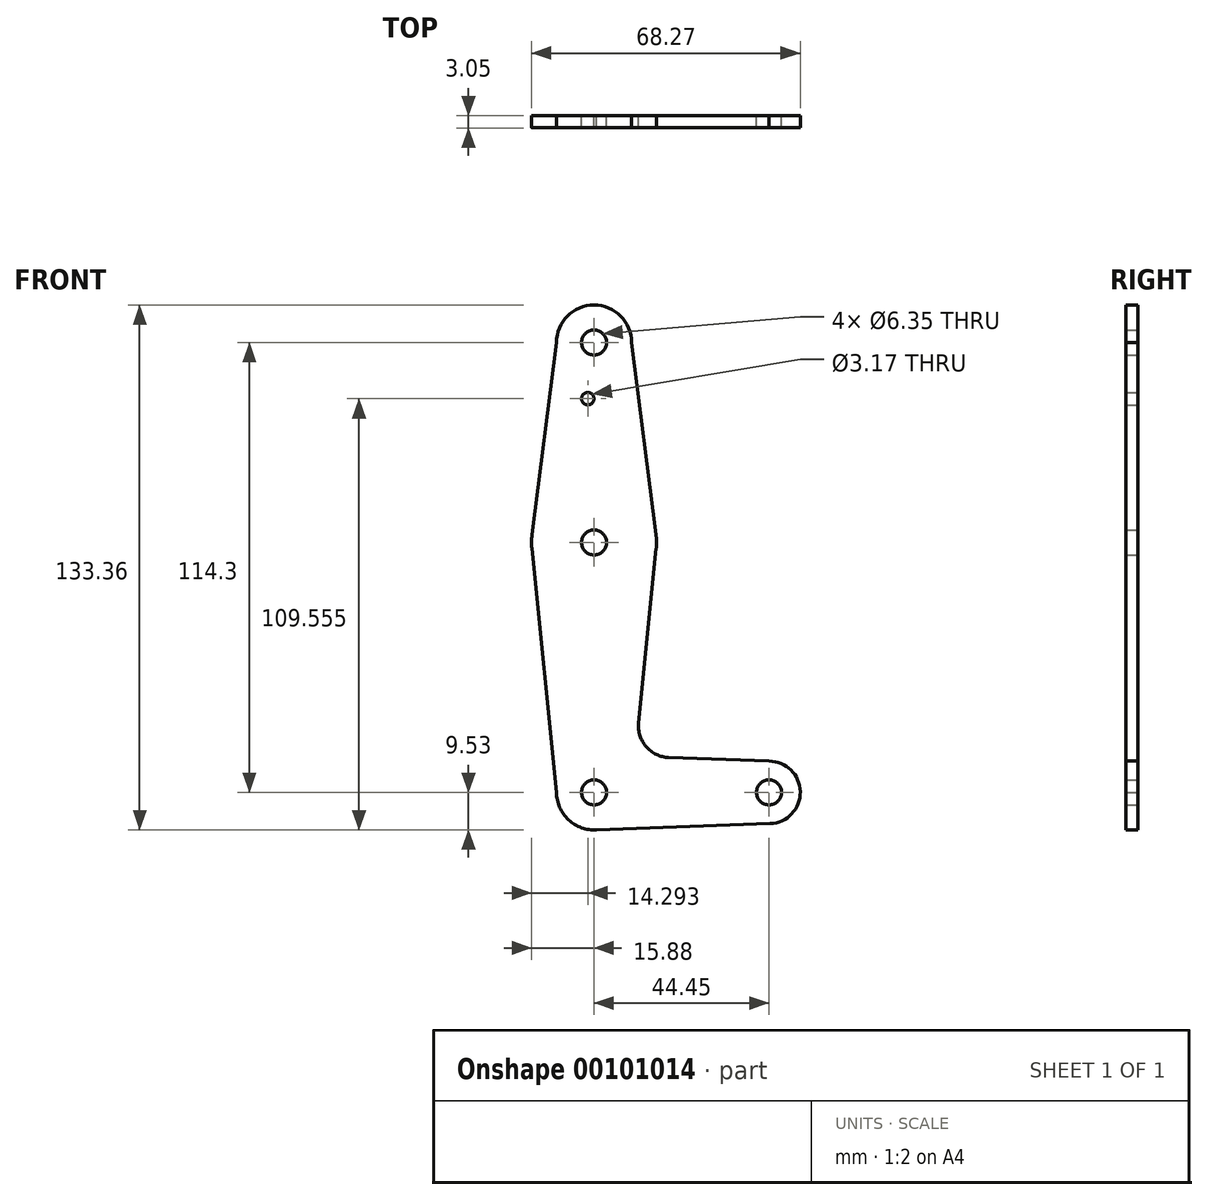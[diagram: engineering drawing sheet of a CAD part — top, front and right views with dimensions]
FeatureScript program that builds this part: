
annotation { "Feature Type Name" : "Feature", "Feature Type Description" : "" }
export const myFeature = defineFeature(function(context is Context, id is Id, definition is map)
    precondition{}
    {
        {
            var Q0;
            Q0=qCreatedBy(makeId("Front.planeOp"),FACE);
            var sketch = newSketch(context, id + "F0", { "sketchPlane" : qUnion([Q0])});
            skCircle(sketch, "E0", {"center": v(0, 0) * mm, "radius": 9.53 * mm});
            skCircle(sketch, "E1", {"center": v(0, 63.5) * mm, "radius": 15.88 * mm});
            skCircle(sketch, "E2", {"center": v(0, 114.3) * mm, "radius": 9.53 * mm});
            skCircle(sketch, "E3", {"center": v(44.45, 0) * mm, "radius": 7.94 * mm});
            skLineSegment(sketch, "E4", {"start": v(0, 0) * mm, "end": v(44.45, 0) * mm, "construction": true});
            skLineSegment(sketch, "E5", {"start": v(0, 0) * mm, "end": v(0, 63.5) * mm, "construction": true});
            skLineSegment(sketch, "E6", {"start": v(0, 114.3) * mm, "end": v(0, 63.5) * mm, "construction": true});
            skLineSegment(sketch, "E7", {"start": v(-9.52, 114.3) * mm, "end": v(-15.75, 65.5) * mm});
            skLineSegment(sketch, "E8", {"start": v(0, -9.53) * mm, "end": v(44.73, -7.93) * mm});
            skLineSegment(sketch, "E9", {"start": v(9.53, 114.3) * mm, "end": v(15.75, 65.5) * mm});
            skCircle(sketch, "E10", {"center": v(0, 114.3) * mm, "radius": 3.18 * mm});
            skCircle(sketch, "E11", {"center": v(0, 63.5) * mm, "radius": 3.18 * mm});
            skCircle(sketch, "E12", {"center": v(0, 0) * mm, "radius": 3.18 * mm});
            skCircle(sketch, "E13", {"center": v(44.45, 0) * mm, "radius": 3.18 * mm});
            skCircle(sketch, "E14", {"center": v(-1.59, 100.03) * mm, "radius": 1.59 * mm});
            skLineSegment(sketch, "E15", {"start": v(11.34, 17.6) * mm, "end": v(15.8, 61.91) * mm});
            skLineSegment(sketch, "E16", {"start": v(44.45, 7.94) * mm, "end": v(18.97, 8.85) * mm});
            skArc(sketch, "E17.filletArc", {"start": v(11.34, 17.6) * mm, "mid": v(13.26, 11.57) * mm, "end": v(18.97, 8.85) * mm});
            skLineSegment(sketch, "E18", {"start": v(-9.53, 0) * mm, "end": v(-15.8, 61.9) * mm});
            skSolve(sketch);
        }
        {
            var Q0;
            Q0 = qSketchRegion(id + "F0", true);
            extrude(context, id + "F1", {"entities" : qUnion([Q0]), "depth" : 3.05 * mm});
        }
    });
